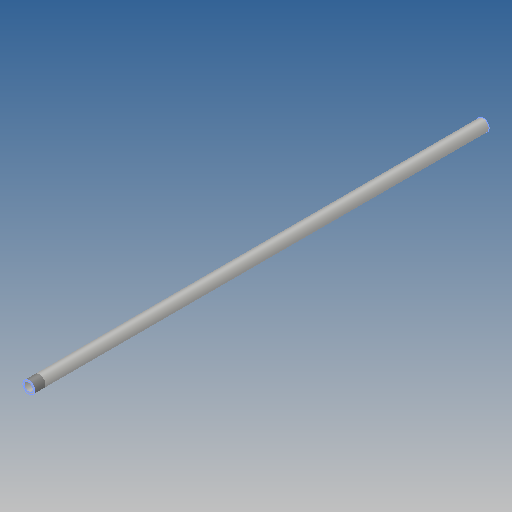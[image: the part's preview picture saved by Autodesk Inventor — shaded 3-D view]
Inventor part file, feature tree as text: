
AUTODESK INVENTOR PART (.ipt)
format: ipt  version: 2019 (Build 230136000, 136)  size: 85,504 bytes
history: native  units: mm
features: extrude x1, other x1, sketch x1
ambient origin geometry x8: Origin, YZ Plane, XZ Plane, XY Plane, X Axis, Y Axis, Z Axis, Center Point
bodies: Solide1 (feature_tree)
feature tree (3):
  extrude  "Extrusion1"  Depth=2.0mm
  other  "Filetage1"
  sketch  "Esquisse1"
